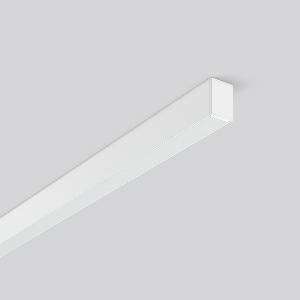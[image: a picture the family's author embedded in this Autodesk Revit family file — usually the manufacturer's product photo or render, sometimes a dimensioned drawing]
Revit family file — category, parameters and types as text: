
# Revit family: less_is_more_27_312199_002_1_7c5a
name_source: partatom
category: Lighting Fixtures
units: mm (PartAtom-declared; Revit-internal decimal feet)

## family parameters
Cut with Voids When Loaded = No
Host = Face
Light Source = No
Part Type = Normal
Room Calculation Point = No
Round Connector Dimension = Use Diameter
Shared = No

## types (1)
- LESS IS MORE 27 (1 x LED Modul 840, 2600 lm, 4000)
    Apparent Load = 31 VA
    CIE Flux Codes = 65 89 98 100 100
    Color Rendering = 80
    Color Temperature = 4000
    Default Elevation = 1800 mm
    Description = Series: LESS IS MORE 27
Ceiling luminaire with slim design. Housing: extruded aluminium profile, powder-coated. End cap aluminium powder-coated. Diffuser made of non-yellowing plastic (PMMA) microprismatic. Suitable for Ceiling mounting, Wall (surface). External driver with connecting cable. 
Colour: traffic white, matt (RAL 9016)
Length: 1212 mm
Width: 28 mm
Height: 38 mm
Lamp: LED
Socket: without socket
Colour temperature: 4000K
Colour rendering index (CRI): 82
System power: 31 W
Rated luminous flux: 2600 lm
Luminous efficiency: 84 lm/W
Control gear: Regulated power supply
Protection class: II
Type of protection: IP 20
    Height = 38 mm
    Lamp = 1 x LED Modul 840
    Lamp Light Flux = 2600 lm
    Lamp count = 1
    Length = 1212 mm
    Lifetime = 50000 h
    Luminous efficacy = 84 lm/W
    Manufacturer = RZB
    ModVariant = No
    Model = 312199.002.1
    Mounting Place = Ceiling, Wall
    Mounting Type = Surface mounted
    Number of Poles = 1
    OnlyDefault = Yes
    Power Factor = 1
    Product Name = LESS IS MORE 27
    Product group = Surface mounted LED linear luminaires
    ProductGroupID = 307
    Protection Class = Protection class II
    Protection Degree = IP 20
    RLX_Detail_Level = 1
    RLX_Emergency_Light_Flux = 0 lm
    RLX_Emergency_Type = 0
    RLX_Emergency_Type_DB = No
    RlxData = <blob elided: 23905 chars, md5=1b9a3a3a>
    Socket = socket
    Standby Power = 0 W
    System Light Flux = 2600 lm
    System Power = 31 W
    Type Comments = Product without accessories
    Type Image = 312196.002.jpg
    URL = http://relux.com
    VarID = ---
    Voltage = 230 V
    Voltage Range = 220-240 V
    Weight = 0.00 kg
    Width = 28 mm

## geometry (parser evidence)
native form markers: Blend x4, Sweep x13
no freeform markers — native parametric forms only
